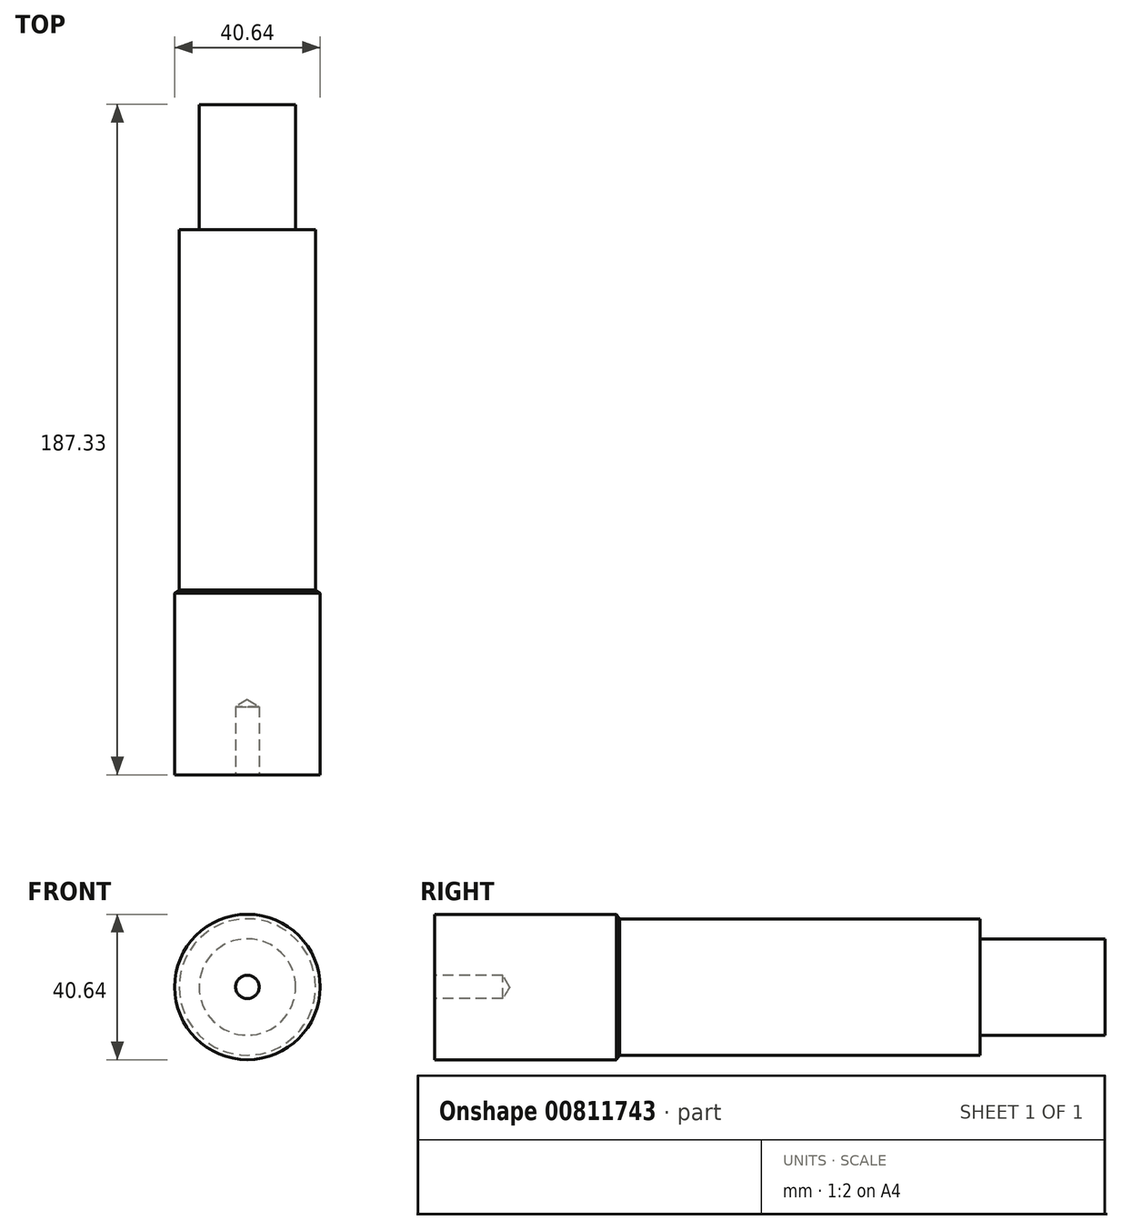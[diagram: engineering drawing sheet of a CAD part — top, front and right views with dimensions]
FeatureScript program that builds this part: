
annotation { "Feature Type Name" : "Feature", "Feature Type Description" : "" }
export const myFeature = defineFeature(function(context is Context, id is Id, definition is map)
    precondition{}
    {
        {
            var Q0;
            Q0=qCreatedBy(makeId("Right.planeOp"),FACE);
            var sketch = newSketch(context, id + "F0", { "sketchPlane" : qUnion([Q0])});
            skLineSegment(sketch, "E0", {"start": v(-82.04, 0) * mm, "end": v(70.36, 0) * mm});
            skLineSegment(sketch, "E1", {"start": v(-82.04, 20.32) * mm, "end": v(-31.24, 20.32) * mm});
            skLineSegment(sketch, "E2", {"start": v(70.36, 13.47) * mm, "end": v(70.36, 19.05) * mm});
            skLineSegment(sketch, "E3", {"start": v(70.36, 13.47) * mm, "end": v(105.29, 13.47) * mm});
            skLineSegment(sketch, "E4", {"start": v(70.36, 19.05) * mm, "end": v(31.75, 19.05) * mm});
            skLineSegment(sketch, "E5", {"start": v(-30.35, 19.05) * mm, "end": v(-31.24, 20.32) * mm});
            skLineSegment(sketch, "E6", {"start": v(70.36, 0) * mm, "end": v(105.29, 0) * mm});
            skLineSegment(sketch, "E7", {"start": v(105.29, 0) * mm, "end": v(105.29, 13.47) * mm});
            skLineSegment(sketch, "E8.trimOffspring", {"start": v(0, 19.05) * mm, "end": v(-30.35, 19.05) * mm});
            skLineSegment(sketch, "E9", {"start": v(31.75, 19.05) * mm, "end": v(0, 19.05) * mm});
            skLineSegment(sketch, "E10", {"start": v(-82.04, 0) * mm, "end": v(-82.04, 5.54) * mm});
            skLineSegment(sketch, "E11", {"start": v(-82.04, 20.32) * mm, "end": v(-82.04, 5.54) * mm});
            skSolve(sketch);
        }
        {
            var Q0;
            Q0=makeQuery(id+"F0.imprint","IMPRINT",FACE,{"disambiguationData":[TD([[makeQuery(id+"F0.imprint","IMPRINT",EDGE,{"derivedFrom":sQuery(id+"F0.wireOp",EDGE,"E0")}),1.0]])]});
            var Q1;
            Q1=sQuery(id+"F0.wireOp",EDGE,"E0");
            revolve(context, id + "F1", {"surfaceOperationType" : NewSurfaceOperationType.NEW, "entities" : qUnion([Q0]), "axis" : qUnion([Q1]), "revolveType" : RevolveType.FULL});
        }
        {
            var Q0;
            Q0=makeQuery(id+"F1.opRevolve","SWEPT_FACE",FACE,{"disambiguationData":[OSD([sQuery(id+"F0.wireOp",EDGE,"E10"),sQuery(id+"F0.wireOp",EDGE,"E11")])]});
            var sketch = newSketch(context, id + "F2", { "sketchPlane" : qUnion([Q0])});
            skPoint(sketch, "E12", {"position": v(0, 0) * mm});
            skSolve(sketch);
        }
        {
            var Q0;
            Q0=sQuery(id+"F2.wireOp",VERTEX,"E12");
            var Q1;
            Q1=makeQuery(id+"F1.opRevolve","SWEPT_BODY",BODY,{"disambiguationData":[OSD([sQuery(id+"F0.wireOp",EDGE,"E0"),sQuery(id+"F0.wireOp",EDGE,"E1"),sQuery(id+"F0.wireOp",EDGE,"E2"),sQuery(id+"F0.wireOp",EDGE,"E3"),sQuery(id+"F0.wireOp",EDGE,"E4"),sQuery(id+"F0.wireOp",EDGE,"E5"),sQuery(id+"F0.wireOp",EDGE,"E6"),sQuery(id+"F0.wireOp",EDGE,"E7"),sQuery(id+"F0.wireOp",EDGE,"E8.trimOffspring"),sQuery(id+"F0.wireOp",EDGE,"E9"),sQuery(id+"F0.wireOp",EDGE,"E10"),sQuery(id+"F0.wireOp",EDGE,"E11")])]});
            hole(context, id + "F3", {"style" : HoleStyle.SIMPLE, "endStyle" : HoleEndStyle.BLIND, "standardTappedOrClearance" : lookupTablePath({ "standard" : "ANSI", "engagement" : "75%", "pitch" : "18 tpi", "size" : "5/16", "type" : "Tapped" }), "standardBlindInLast" : lookupTablePath({ "standard" : "ANSI", "fit" : "Free", "engagement" : "75%", "pitch" : "18 tpi", "size" : "5/16", "type" : "Clearance & tapped" }), "holeDiameter" : 6.53 * mm, "majorDiameter" : 7.94 * mm, "showTappedDepth" : true, "holeDepth" : 19.05 * mm, "tappedDepth" : 14.82 * mm, "tapClearance" : 3, "startFromSketch" : true, "locations" : qUnion([Q0]), "scope" : qUnion([Q1])});
        }
    });
